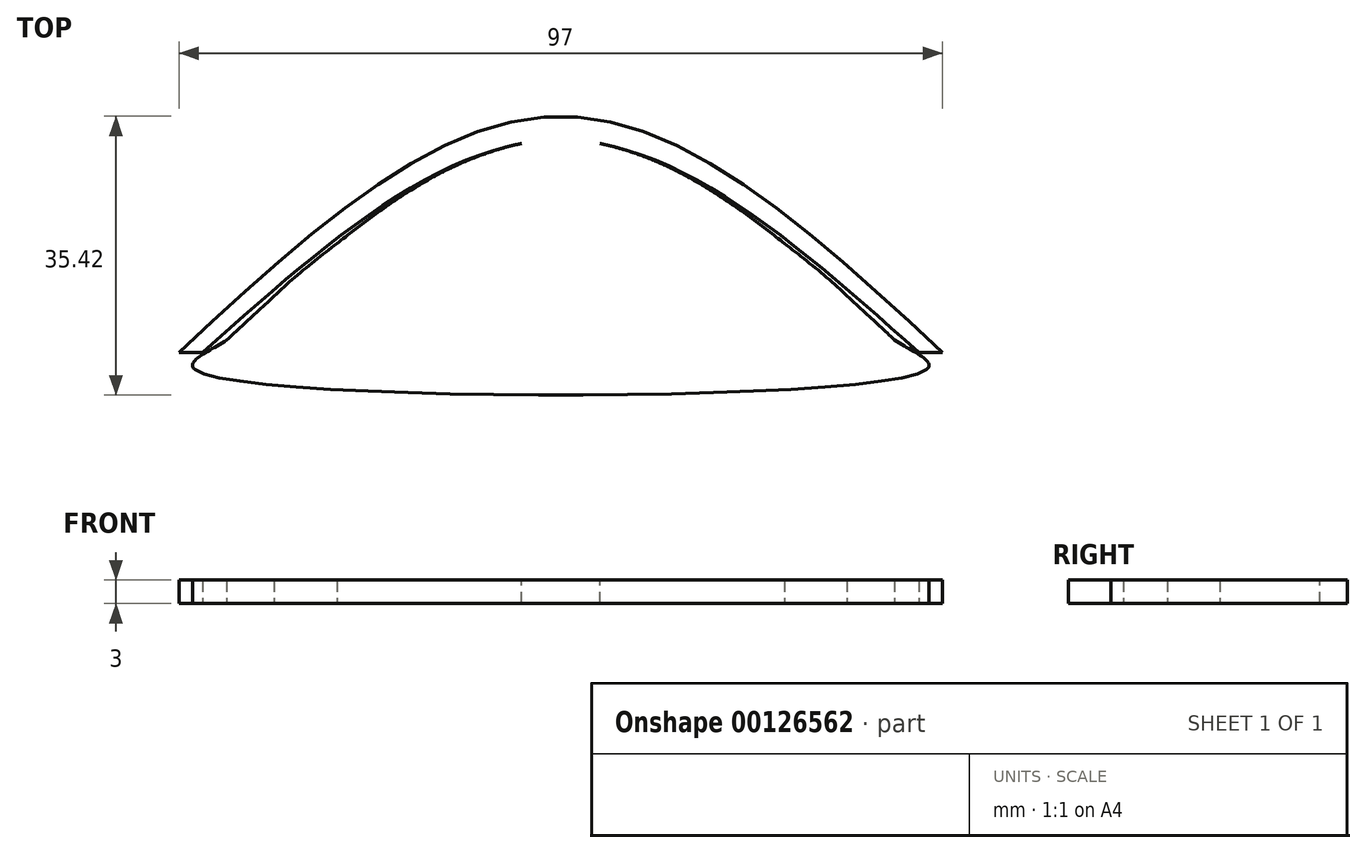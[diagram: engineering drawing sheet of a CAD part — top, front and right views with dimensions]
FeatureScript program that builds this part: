
annotation { "Feature Type Name" : "Feature", "Feature Type Description" : "" }
export const myFeature = defineFeature(function(context is Context, id is Id, definition is map)
    precondition{}
    {
        {
            var Q0;
            Q0=qCreatedBy(makeId("Top.planeOp"),FACE);
            var sketch = newSketch(context, id + "F0", { "sketchPlane" : qUnion([Q0])});
            skFitSpline(sketch, "E0", {"points": [v(-48.5, 0) * mm, v(0, 30) * mm, v(48.5, 0) * mm], "startDerivative": vector(97, 90) * mm, "endDerivative": vector(97, -90) * mm});
            skLineSegment(sketch, "E1.0", {"start": v(-40.83, 3) * mm, "end": v(-40.83, 3) * mm});
            skLineSegment(sketch, "E1.1", {"start": v(40.83, 3) * mm, "end": v(40.83, 3) * mm});
            skFitSpline(sketch, "E1.2", {"points": [v(-46.46, -2.2) * mm, v(-42.42, 1.55) * mm, v(-36.39, 7.14) * mm, v(-28.43, 13.83) * mm, v(-22.52, 18.29) * mm, v(-16.7, 22) * mm, v(-11.93, 24.35) * mm, v(-8.19, 25.7) * mm, v(-5.42, 26.44) * mm, v(-3.15, 26.82) * mm, v(-1.34, 26.97) * mm, v(0, 27.01) * mm, v(1.34, 26.97) * mm, v(3.15, 26.82) * mm, v(5.42, 26.44) * mm, v(8.19, 25.7) * mm, v(11.93, 24.35) * mm, v(16.7, 22) * mm, v(22.52, 18.29) * mm, v(28.43, 13.83) * mm, v(36.39, 7.14) * mm, v(42.42, 1.55) * mm, v(46.46, -2.2) * mm, v(-46.46, -2.2) * mm]});
            skFitSpline(sketch, "E2", {"points": [v(-45.5, 0) * mm, v(0, 27) * mm, v(45.5, 0) * mm], "startDerivative": vector(91, 81) * mm, "endDerivative": vector(91, -81) * mm});
            skFitSpline(sketch, "E3.trimOffspring", {"points": [v(-46.46, -2.2) * mm, v(-42.42, 1.55) * mm, v(-36.39, 7.14) * mm, v(-28.43, 13.83) * mm, v(-22.52, 18.29) * mm, v(-16.7, 22) * mm, v(-11.93, 24.35) * mm, v(-8.19, 25.7) * mm, v(-5.42, 26.44) * mm, v(-3.15, 26.82) * mm, v(-1.34, 26.97) * mm, v(0, 27.01) * mm, v(1.34, 26.97) * mm, v(3.15, 26.82) * mm, v(5.42, 26.44) * mm, v(8.19, 25.7) * mm, v(11.93, 24.35) * mm, v(16.7, 22) * mm, v(22.52, 18.29) * mm, v(28.43, 13.83) * mm, v(36.39, 7.14) * mm, v(42.42, 1.55) * mm, v(46.46, -2.2) * mm]});
            skLineSegment(sketch, "E4", {"start": v(45.5, 0) * mm, "end": v(48.5, 0) * mm});
            skLineSegment(sketch, "E5", {"start": v(-48.5, 0) * mm, "end": v(-45.5, 0) * mm});
            skSolve(sketch);
        }
        {
            var Q0;
            Q0=qSketchRegion(id+"F0",true);
            extrude(context, id + "F1", {"entities" : qUnion([Q0]), "endBound" : BoundingType.SYMMETRIC, "depth" : 3 * mm});
        }
    });
